# Revit family: DAL_A3-AGI-Hurricane-Sliding-Door-1524X2032
name_source: partatom
category: Doors
revit_build: Autodesk Revit 2016 (Build: 20150220_1215(x64)
units: mm (PartAtom-declared; Revit-internal decimal feet)

## family parameters
Always vertical = Yes
Cut with Voids When Loaded = No
Host = Wall
Room Calculation Point = No
Shared = No

## types (1)
- AGI HURRICANE SLIDING DOOR 1524 X2032
    Frame = Aluminium
    Frame Projection Ext. = 25 mm  [stored 0.082021 ft]
    Frame Projection Int. = 25 mm  [stored 0.082021 ft]
    Frame Width = 75 mm  [stored 0.246063 ft]
    Function = Interior
    Glass = Glass
    Height = 2032 mm
    Manufacturer = AGI
    Panel Height = 1972 mm
    Panel Width = 762 mm  [stored 2.5 ft]
    URL = www.agi.co.za
    Wall Closure = By host
    Width = 1524 mm  [stored 5 ft]

note: [stored X ft] marks values corroborated as IEEE doubles in the binary element streams (Revit-internal decimal feet)

## geometry (parser evidence)
native form markers: Sweep x8
no freeform markers — native parametric forms only
